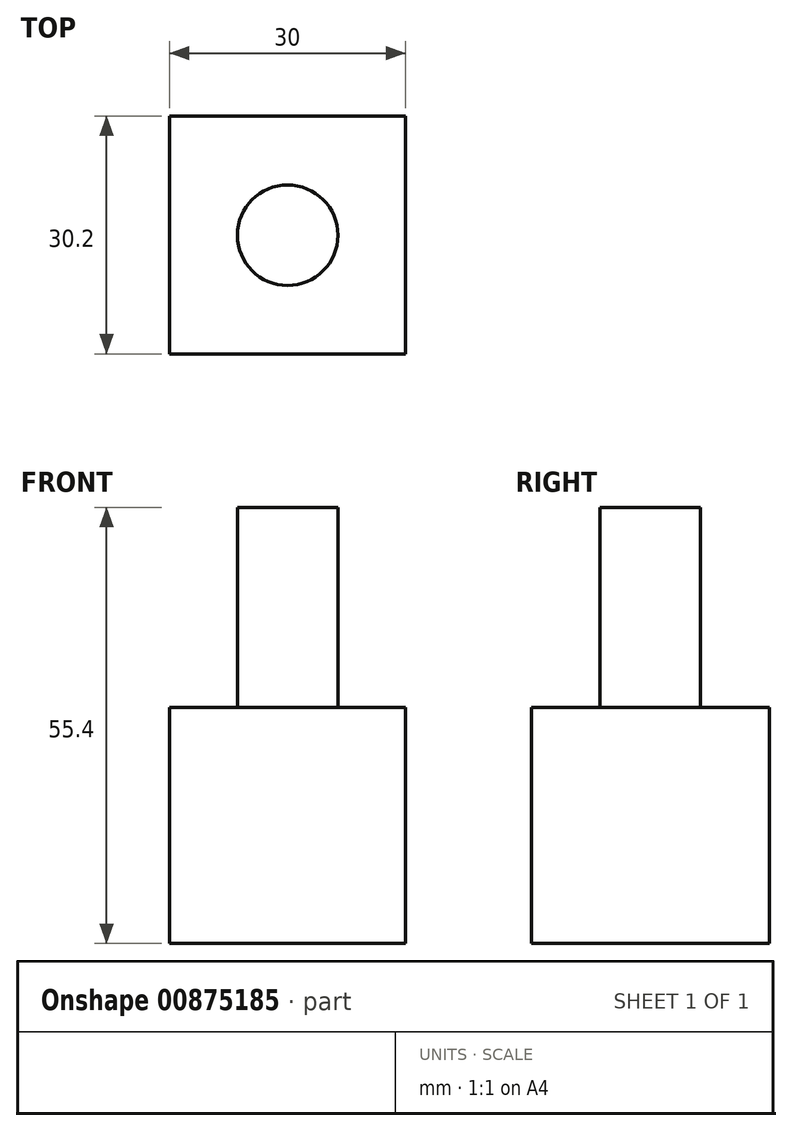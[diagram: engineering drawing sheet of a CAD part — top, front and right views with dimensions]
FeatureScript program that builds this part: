
annotation { "Feature Type Name" : "Feature", "Feature Type Description" : "" }
export const myFeature = defineFeature(function(context is Context, id is Id, definition is map)
    precondition{}
    {
        {
            var Q0;
            Q0=qCreatedBy(makeId("Front.planeOp"),FACE);
            var sketch = newSketch(context, id + "F0", { "sketchPlane" : qUnion([Q0])});
            skLineSegment(sketch, "E0.bottom", {"start": v(-15, 15) * mm, "end": v(15, 15) * mm});
            skLineSegment(sketch, "E0.top", {"start": v(-15, -15) * mm, "end": v(15, -15) * mm});
            skLineSegment(sketch, "E0.left", {"start": v(-15, 15) * mm, "end": v(-15, -15) * mm});
            skLineSegment(sketch, "E0.right", {"start": v(15, 15) * mm, "end": v(15, -15) * mm});
            skPoint(sketch, "E0.middle", {"position": v(0, 0) * mm});
            skSolve(sketch);
        }
        {
            var Q0;
            Q0=makeQuery(id+"F0.imprint","IMPRINT",FACE,{"disambiguationData":[TD([[makeQuery(id+"F0.imprint","IMPRINT",EDGE,{"derivedFrom":sQuery(id+"F0.wireOp",EDGE,"E0.bottom")}),-1.0]])]});
            extrude(context, id + "F1", {"entities" : qUnion([Q0]), "depth" : 30.2 * mm, "offsetDistance" : 25.4 * mm});
        }
        {
            var Q0;
            Q0=makeQuery(id+"F1.opExtrude","SWEPT_FACE",FACE,{"disambiguationData":[OSD([sQuery(id+"F0.wireOp",EDGE,"E0.bottom")])]});
            var sketch = newSketch(context, id + "F2", { "sketchPlane" : qUnion([Q0])});
            skCircle(sketch, "E1", {"center": v(0, -15.14) * mm, "radius": 6.38 * mm});
            skSolve(sketch);
        }
        {
            var Q0;
            Q0=makeQuery(id+"F2.imprint","IMPRINT",FACE,{"disambiguationData":[TD([[makeQuery(id+"F2.imprint","IMPRINT",EDGE,{"derivedFrom":sQuery(id+"F2.wireOp",EDGE,"E1")}),1.0]])]});
            var Q1;
            Q1=sQuery(id+"F2.wireOp",EDGE,"E1");
            extrude(context, id + "F3", {"entities" : qUnion([Q0]), "operationType" : NewBodyOperationType.ADD, "surfaceEntities" : qUnion([Q1]), "depth" : 25.4 * mm, "offsetDistance" : 25.4 * mm});
        }
    });
